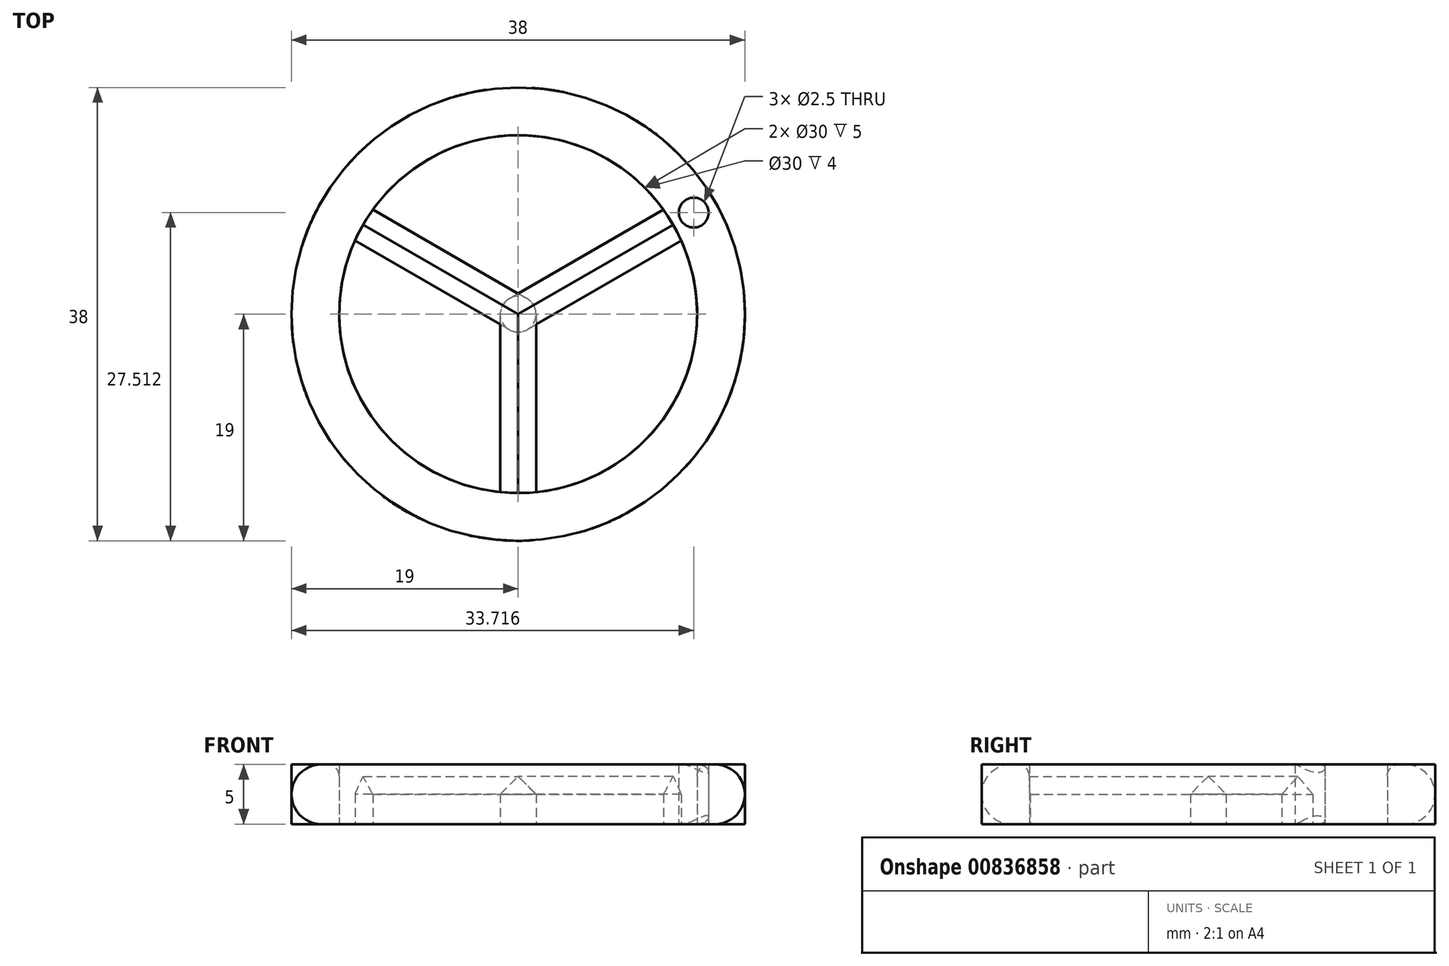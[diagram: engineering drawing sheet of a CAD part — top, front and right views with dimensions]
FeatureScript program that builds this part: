
annotation { "Feature Type Name" : "Feature", "Feature Type Description" : "" }
export const myFeature = defineFeature(function(context is Context, id is Id, definition is map)
    precondition{}
    {
        {
            var Q0;
            Q0=qCreatedBy(makeId("Top.planeOp"),FACE);
            var sketch = newSketch(context, id + "F0", { "sketchPlane" : qUnion([Q0])});
            skCircle(sketch, "E0", {"center": v(0, 0) * mm, "radius": 15 * mm});
            skCircle(sketch, "E1", {"center": v(0, 0) * mm, "radius": 1.5 * mm});
            skLineSegment(sketch, "E2", {"start": v(-1.5, 0) * mm, "end": v(-1.5, -14.92) * mm});
            skLineSegment(sketch, "E3", {"start": v(1.5, 0) * mm, "end": v(1.5, -14.92) * mm});
            skCircle(sketch, "E4", {"center": v(0, 0) * mm, "radius": 19 * mm});
            skSolve(sketch);
        }
        {
            var Q0;
            Q0 = qSketchRegion(id + "F0", true);
            var Q1;
            {var subQ0=sQuery(id+"F0.wireOp",EDGE,"inIqQuvG-b72C-jRXI-krPL-7P3bYnRmSngq");var subQ1=sQuery(id+"F0.wireOp",EDGE,"E4");var subQ2=makeQuery(id+"F0.imprint","INTERSECT",VERTEX,{"disambiguationData":[OD(0.0)],"derivedFrom":[subQ1,subQ0]});Q1=makeQuery(id+"F0.imprint","IMPRINT",FACE,{"disambiguationData":[TD([[makeQuery(id+"F0.imprint","IMPRINT",EDGE,{"disambiguationData":[TD([[subQ2,-1.0]])],"derivedFrom":subQ1}),1.0]])]});}
            extrude(context, id + "F1", {"entities" : qUnion([Q0, Q1]), "depth" : 5 * mm, "offsetDistance" : 25 * mm});
        }
        {
            var Q0;
            {var subQ0=sQuery(id+"F0.wireOp",EDGE,"E1");var subQ1=makeQuery(id+"F0.imprint","INTERSECT",VERTEX,{"derivedFrom":[subQ0,sQuery(id+"F0.wireOp",EDGE,"E2")]});Q0=makeQuery(id+"F0.imprint","IMPRINT",FACE,{"disambiguationData":[TD([[makeQuery(id+"F0.imprint","IMPRINT",EDGE,{"disambiguationData":[TD([[subQ1,1.0]])],"derivedFrom":subQ0}),1.0]])]});}
            var Q1;
            {var subQ0=sQuery(id+"F0.wireOp",EDGE,"E2");Q1=makeQuery(id+"F0.imprint","IMPRINT",FACE,{"disambiguationData":[TD([[makeQuery(id+"F0.imprint","IMPRINT",EDGE,{"derivedFrom":subQ0}),1.0]])]});}
            extrude(context, id + "F2", {"entities" : qUnion([Q0, Q1]), "operationType" : NewBodyOperationType.ADD, "depth" : 4 * mm, "offsetDistance" : 25 * mm});
        }
        {
            var Q0;
            Q0=makeQuery(id+"F1.opExtrude","SWEPT_BODY",BODY,{"disambiguationData":[OSD([sQuery(id+"F0.wireOp",EDGE,"E0"),sQuery(id+"F0.wireOp",EDGE,"E4")])]});
            var Q1;
            Q1=sQuery(id+"F0.wireOp",EDGE,"E1");
            circularPattern(context, id + "F3", {"entities" : qUnion([Q0]), "axis" : qUnion([Q1]), "angle" : 360 * degree, "instanceCount" : 3, "equalSpace" : true});
        }
        {
            var Q0;
            Q0=makeQuery(id+"F3.opPattern","COPY",EDGE,{"derivedFrom":makeQuery(id+"F2.opExtrude","CAP_EDGE",EDGE,{"disambiguationData":[OSD([sQuery(id+"F0.wireOp",EDGE,"E3")])],"isStart":false}),"instanceName":"2"});
            var Q1;
            Q1=makeQuery(id+"F3.opPattern","COPY",EDGE,{"derivedFrom":makeQuery(id+"F2.opExtrude","CAP_EDGE",EDGE,{"disambiguationData":[OSD([sQuery(id+"F0.wireOp",EDGE,"E2")])],"isStart":false}),"instanceName":"2"});
            var Q2;
            Q2=makeQuery(id+"F2.opExtrude","CAP_EDGE",EDGE,{"disambiguationData":[OSD([sQuery(id+"F0.wireOp",EDGE,"E2")])],"isStart":false});
            var Q3;
            Q3=makeQuery(id+"F2.opExtrude","CAP_EDGE",EDGE,{"disambiguationData":[OSD([sQuery(id+"F0.wireOp",EDGE,"E3")])],"isStart":false});
            var Q4;
            Q4=makeQuery(id+"F3.opPattern","COPY",EDGE,{"derivedFrom":makeQuery(id+"F2.opExtrude","CAP_EDGE",EDGE,{"disambiguationData":[OSD([sQuery(id+"F0.wireOp",EDGE,"E2")])],"isStart":false}),"instanceName":"1"});
            var Q5;
            Q5=makeQuery(id+"F3.opPattern","COPY",EDGE,{"derivedFrom":makeQuery(id+"F2.opExtrude","CAP_EDGE",EDGE,{"disambiguationData":[OSD([sQuery(id+"F0.wireOp",EDGE,"E3")])],"isStart":false}),"instanceName":"1"});
            chamfer(context, id + "F4", {"entities" : qUnion([Q0, Q1, Q2, Q3, Q4, Q5]), "width" : 1.5 * mm, "tangentPropagation" : true});
        }
        {
            var Q0;
            Q0=makeQuery(id+"F3.opPattern","COPY",EDGE,{"derivedFrom":makeQuery(id+"F1.opExtrude","CAP_EDGE",EDGE,{"disambiguationData":[OSD([sQuery(id+"F0.wireOp",EDGE,"E0")])],"isStart":false}),"instanceName":"2"});
            fillet(context, id + "F5", {"entities" : qUnion([Q0]), "radius" : 1 * mm, "tangentPropagation" : true, "allowEdgeOverflow" : false});
        }
        {
            var Q0;
            Q0=makeQuery(id+"F3.opPattern","COPY",EDGE,{"derivedFrom":makeQuery(id+"F1.opExtrude","CAP_EDGE",EDGE,{"disambiguationData":[OSD([sQuery(id+"F0.wireOp",EDGE,"E4")])],"isStart":false}),"instanceName":"2"});
            var Q1;
            Q1=makeQuery(id+"F3.opPattern","COPY",EDGE,{"derivedFrom":makeQuery(id+"F1.opExtrude","CAP_EDGE",EDGE,{"disambiguationData":[OSD([sQuery(id+"F0.wireOp",EDGE,"E4")])],"isStart":true}),"instanceName":"2"});
            fillet(context, id + "F6", {"entities" : qUnion([Q0, Q1]), "radius" : 2.5 * mm, "tangentPropagation" : true, "allowEdgeOverflow" : false});
        }
        {
            var Q0;
            Q0=qCreatedBy(makeId("Top.planeOp"),FACE);
            var sketch = newSketch(context, id + "F7", { "sketchPlane" : qUnion([Q0])});
            skCircle(sketch, "E5", {"center": v(14.72, 8.51) * mm, "radius": 1.25 * mm});
            skSolve(sketch);
        }
        {
            var Q0;
            Q0 = qSketchRegion(id + "F7", true);
            extrude(context, id + "F8", {"entities" : qUnion([Q0]), "operationType" : NewBodyOperationType.REMOVE, "depth" : 5 * mm, "offsetDistance" : 25 * mm});
        }
    });
